# Revit family: Magnus 2030mm
name_source: partatom
category: Lighting Fixtures
revit_build: Autodesk Revit 2017 (Build: 20190508_0315(x64)
units: mm (PartAtom-declared; Revit-internal decimal feet)

## family parameters
Always vertical = No
Cut with Voids When Loaded = No
Light Source = No
Part Type = Normal
Room Calculation Point = No
Round Connector Dimension = Use Diameter
Shared = No
Work Plane-Based = No

## types (6) — shared parameters
Apparent Load = 11 VA
Article Number = On Request
Assembly Code = 63.0
Description = Veko Lightline
IK Value = *User Defined
IP Value = *User Defined
IfcExportAs = IfcLightFixtureType
IfcExportType = POINTSOURCE
Lamp = LED
Manufacturer = Veko Lightsystems
URL = https://www.veko.com
Wattage Comments = Load can vary between 11,3 - 122,4(W)

## per-type parameters (varying)
| type | Model | Selected Optic |
| Narrow | Magnus Narrow | Optics : Narrow |
| Semi Wide | Magnus Semi Wide | Optics : Semi Wide |
| Wide | Magnus Wide | Optics : Wide |
| X-Wide | Magnus X-Wide | Optics : X-Wide |
| Diffuse | Magnus Diffuse | Optics : Diffuse |
| Circular | Magnus Circular | Optics : Circular |

## geometry (parser evidence)
native form markers: Sweep x50
no freeform markers — native parametric forms only
